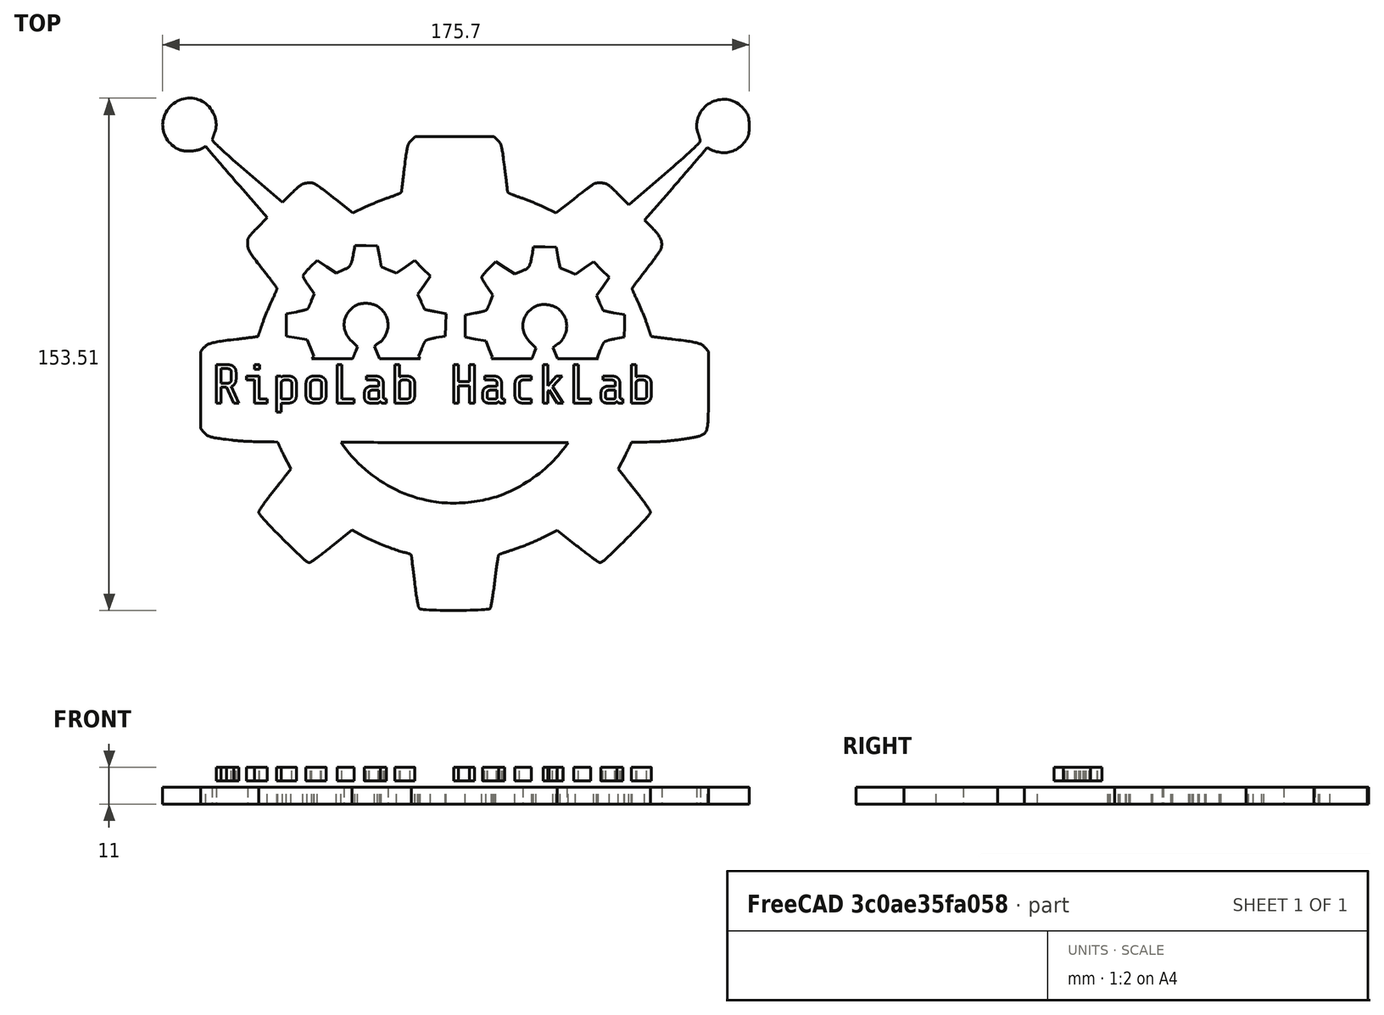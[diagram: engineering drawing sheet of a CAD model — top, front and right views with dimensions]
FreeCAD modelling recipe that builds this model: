
FCSTD DOCUMENT  (FreeCAD 0.15R4671 (Git))
Label: logo_3d
License: All rights reserved
LicenseURL: http://es.wikipedia.org/wiki/Todos_los_derechos_reservados
objects: Part::Feature×6, Part::Extrusion×3, Part::Cut×2, Part::MultiFuse×1, Part::Part2DObjectPython×1
note: 13 computed .brp shape members not serialized (recipe doc carries the construction recipe); baked Part::Feature solids carry a one-line shape summary decoded from their .brp

FEATURE [Part::Feature] path3415
  Placement = pos=(0,659.362,0) rot=(0,0,1;0rad)
  shape: bbox 117.4 x 51.57 x 2e-07 mm, 1 faces, 0 solids (baked)
FEATURE [Part::Feature] path3415001
  Placement = pos=(0,652.362,0) rot=(0,0,1;0rad)
  shape: bbox 176.2 x 103.8 x 2e-07 mm, 1 faces, 0 solids (baked)
FEATURE [Part::Feature] path3415002
  Placement = pos=(0,652.362,0) rot=(0,0,1;0rad)
  shape: bbox 47.84 x 42.86 x 2e-07 mm, 1 faces, 0 solids (baked)
FEATURE [Part::Feature] path3415003
  Placement = pos=(0,652.362,0) rot=(0,0,1;0rad)
  shape: bbox 47.84 x 42.86 x 2e-07 mm, 1 faces, 0 solids (baked)
FEATURE [Part::Feature] rect3550
  Placement = pos=(0,652.362,0) rot=(0,0,1;0rad)
  shape: bbox 106.5 x 12.59 x 2e-07 mm, 1 faces, 0 solids (baked)
FEATURE [Part::Cut] Cut
  Base = -> path3415001
  Tool = -> path3415002
FEATURE [Part::Cut] Cut001
  Base = -> Cut
  Tool = -> path3415003
FEATURE [Part::MultiFuse] Fusion
  Shapes = -> [rect3550,path3415,Cut001]
FEATURE [Part::Feature] Fusion001
  shape: bbox 176.2 x 154.3 x 2e-07 mm, 1 faces, 0 solids (baked)
FEATURE [Part::Extrusion] Extrude
  Base = -> Fusion001
  Dir = (0,0,5)
  Solid = true
FEATURE [Part::Extrusion] Extrude001
  Base = -> Fusion001
  Dir = (0,0,5)
  Solid = true
FEATURE [Part::Part2DObjectPython] ShapeString  # Draft 2D object (typed FeaturePython)
  FontFile = <userpath>/devs/ripolab/fonts/Share_Tech_Mono/ShareTechMono-Regular.ttf
  Placement = pos=(-40,12,0) rot=(0,0,1;0rad)
  Size = 6
  String = RipoLab HackLab
  Tracking = 0
FEATURE [Part::Extrusion] Extrude002
  Base = -> ShapeString
  Dir = (0,0,4)
  Placement = pos=(57,-118,7) rot=(0,0,1;0rad)
  Solid = true
